# Revit family: HVAC_Air-Conditioning_Ice-Air_SPXC
name_source: partatom
category: Mechanical Equipment
units: mm (PartAtom-declared; Revit-internal decimal feet)

## family parameters
Always vertical = Yes
Cut with Voids When Loaded = No
OmniClass Number = 23.75.10.21.11
Part Type = Normal
Room Calculation Point = No
Round Connector Dimension = Use Diameter
Shared = No
Work Plane-Based = No

## types (12) — shared parameters
Description = SPXC Series Single Package Air Conditioner and Heat Pump
Drain Pipe Diameter = 1 "
Frequency = 60 Hz
HSPF = 9
Manufacturer = Ice Air
Outside Air = 60 CFM
Phase = 1
Power Factor = 1
Product Material = Ice Air - Metal - Aluminium
Product Page URL = https://www.ice-air.com
Supply Air Connection Width = 9.5 "
URL = https://www.ice-air.com
Voltage = 208 V
z_Supply Pipe Center = 2 "
zero-valued in all types: Default Elevation

## per-type parameters (varying)
- SPXC12-3.5kW: Airflow=400 CFM; Apparent Load=1040 VA; COP=3.5; COP @ -5°F=1.52; COP @ 10°F=2.04; COP @ 5°F=1.86; Cooling Capacity Range=9,700 - 16,700; Electric Heater=3500 VA; Electric Heater (A)=17 A; Energy Efficiency Rating=13; Heating Capacity @ -5°F=5,100; Heating Capacity @ 10°F=7,100; Heating Capacity @ 5°F=6,800; Heating Capacity Range=8,600 - 14,200; Heating Input=5 A; Heating Input (Watts)=955 W; Height=47 "; Length=23 "; MCA (with Electric Heat)=22.5; MOCP (with Electric Heat)=25; Sensible Cooling Capacity=9900 Btu/h; Supply Air Connection Depth=8.5 "; Total Cooling Capacity=11200 Btu/h; Total Heating Capacity=11400 Btu/h; Weight=1 kN; Width=23 "
- SPXC12-5.0kW: Airflow=400 CFM; Apparent Load=1040 VA; COP=3.5; COP @ -5°F=1.52; COP @ 10°F=2.04; COP @ 5°F=1.86; Cooling Capacity Range=9,700 - 16,700; Electric Heater=5000 VA; Electric Heater (A)=24 A; Energy Efficiency Rating=13; Heating Capacity @ -5°F=5,100; Heating Capacity @ 10°F=7,100; Heating Capacity @ 5°F=6,800; Heating Capacity Range=8,600 - 14,200; Heating Input=5 A; Heating Input (Watts)=955 W; Height=47 "; Length=23 "; MCA (with Electric Heat)=27.8; MOCP (with Electric Heat)=30; Sensible Cooling Capacity=9900 Btu/h; Supply Air Connection Depth=8.5 "; Total Cooling Capacity=11200 Btu/h; Total Heating Capacity=11400 Btu/h; Weight=1 kN; Width=23 "
- SPXC18-5.0kW: Airflow=600 CFM; Apparent Load=1456 VA; COP=3.3; COP @ -5°F=1.5; COP @ 10°F=1.99; COP @ 5°F=1.82; Cooling Capacity Range=10,500 - 19,500; Electric Heater=5000 VA; Electric Heater (A)=24 A; Energy Efficiency Rating=11; Heating Capacity @ -5°F=8,000; Heating Capacity @ 10°F=10,700; Heating Capacity @ 5°F=10,300; Heating Capacity Range=11,500 - 19,200; Heating Input=7 A; Heating Input (Watts)=1350 W; Height=47 "; Length=23 "; MCA (with Electric Heat)=28.7; MOCP (with Electric Heat)=30; Sensible Cooling Capacity=12900 Btu/h; Supply Air Connection Depth=8.5 "; Total Cooling Capacity=16800 Btu/h; Total Heating Capacity=15200 Btu/h; Weight=1.2 kN; Width=23 "
- SPXC18-7.5kW: Airflow=600 CFM; Apparent Load=1456 VA; COP=3.3; COP @ -5°F=1.5; COP @ 10°F=1.99; COP @ 5°F=1.82; Cooling Capacity Range=10,500 - 19,500; Electric Heater=7500 VA; Electric Heater (A)=36 A; Energy Efficiency Rating=11; Heating Capacity @ -5°F=8,000; Heating Capacity @ 10°F=10,700; Heating Capacity @ 5°F=10,300; Heating Capacity Range=11,500 - 19,200; Heating Input=7 A; Heating Input (Watts)=1350 W; Height=47 "; Length=23 "; MCA (with Electric Heat)=47.4; MOCP (with Electric Heat)=50; Sensible Cooling Capacity=12900 Btu/h; Supply Air Connection Depth=8.5 "; Total Cooling Capacity=16800 Btu/h; Total Heating Capacity=15200 Btu/h; Weight=1.2 kN; Width=23 "
- SPXC24-5.0kW: Airflow=800 CFM; Apparent Load=1872 VA; COP=3.3; COP @ -5°F=1.72; COP @ 10°F=2.18; COP @ 5°F=1.99; Cooling Capacity Range=13,900 - 25,600; Electric Heater=5000 VA; Electric Heater (A)=24 A; Energy Efficiency Rating=11; Heating Capacity @ -5°F=15,800; Heating Capacity @ 10°F=17,400; Heating Capacity @ 5°F=16,200; Heating Capacity Range=15,100 - 25,900; Heating Input=9 A; Heating Input (Watts)=1865 W; Height=64 "; Length=26 "; MCA (with Electric Heat)=28.9; MOCP (with Electric Heat)=30; Sensible Cooling Capacity=18500 Btu/h; Supply Air Connection Depth=10.63 "; Total Cooling Capacity=24000 Btu/h; Total Heating Capacity=21000 Btu/h; Weight=1.6 kN; Width=28 "
- SPXC24-7.5kW: Airflow=800 CFM; Apparent Load=1872 VA; COP=3.3; COP @ -5°F=1.72; COP @ 10°F=2.18; COP @ 5°F=1.99; Cooling Capacity Range=13,900 - 25,600; Electric Heater=7500 VA; Electric Heater (A)=36 A; Energy Efficiency Rating=11; Heating Capacity @ -5°F=15,800; Heating Capacity @ 10°F=17,400; Heating Capacity @ 5°F=16,200; Heating Capacity Range=15,100 - 25,900; Heating Input=9 A; Heating Input (Watts)=1865 W; Height=64 "; Length=26 "; MCA (with Electric Heat)=47.8; MOCP (with Electric Heat)=50; Sensible Cooling Capacity=18500 Btu/h; Supply Air Connection Depth=10.63 "; Total Cooling Capacity=24000 Btu/h; Total Heating Capacity=21000 Btu/h; Weight=1.6 kN; Width=28 "
- SPXC30-5.0kW: Airflow=1000 CFM; Apparent Load=2496 VA; COP=3.3; COP @ -5°F=1.69; COP @ 10°F=2.15; COP @ 5°F=1.96; Cooling Capacity Range=16,600 - 30,800; Electric Heater=5000 VA; Electric Heater (A)=24 A; Energy Efficiency Rating=11; Heating Capacity @ -5°F=19,300; Heating Capacity @ 10°F=21,300; Heating Capacity @ 5°F=19,800; Heating Capacity Range=18,000 - 31,500; Heating Input=12 A; Heating Input (Watts)=2509 W; Height=64 "; Length=26 "; MCA (with Electric Heat)=30.8; MOCP (with Electric Heat)=35; Sensible Cooling Capacity=22500 Btu/h; Supply Air Connection Depth=10.63 "; Total Cooling Capacity=27500 Btu/h; Total Heating Capacity=26000 Btu/h; Weight=1.7 kN; Width=28 "
- SPXC30-7.5kW: Airflow=1000 CFM; Apparent Load=2496 VA; COP=3.3; COP @ -5°F=1.69; COP @ 10°F=2.15; COP @ 5°F=1.96; Cooling Capacity Range=16,600 - 30,800; Electric Heater=7500 VA; Electric Heater (A)=36 A; Energy Efficiency Rating=11; Heating Capacity @ -5°F=19,300; Heating Capacity @ 10°F=21,300; Heating Capacity @ 5°F=19,800; Heating Capacity Range=18,000 - 31,500; Heating Input=12 A; Heating Input (Watts)=2509 W; Height=64 "; Length=26 "; MCA (with Electric Heat)=49.6; MOCP (with Electric Heat)=50; Sensible Cooling Capacity=22500 Btu/h; Supply Air Connection Depth=10.63 "; Total Cooling Capacity=27500 Btu/h; Total Heating Capacity=26000 Btu/h; Weight=1.7 kN; Width=28 "
- SPXC12: Airflow=400 CFM; Apparent Load=1040 VA; COP=3.5; COP @ -5°F=1.52; COP @ 10°F=2.04; COP @ 5°F=1.86; Cooling Capacity Range=9,700 - 16,700; Electric Heater=0 VA; Electric Heater (A)=0 A; Energy Efficiency Rating=13; Heating Capacity @ -5°F=5,100; Heating Capacity @ 10°F=7,100; Heating Capacity @ 5°F=6,800; Heating Capacity Range=8,600 - 14,200; Heating Input=5 A; Heating Input (Watts)=955 W; Height=47 "; Length=23 "; MCA (without Electric Heat)=9.8; MOCP (without Electric Heat)=15; Sensible Cooling Capacity=9900 Btu/h; Supply Air Connection Depth=8.5 "; Total Cooling Capacity=11200 Btu/h; Total Heating Capacity=11400 Btu/h; Weight=1 kN; Width=23 "
- SPXC18: Airflow=600 CFM; Apparent Load=1456 VA; COP=3.3; COP @ -5°F=1.5; COP @ 10°F=1.99; COP @ 5°F=1.82; Cooling Capacity Range=10,500 - 19,500; Electric Heater=0 VA; Electric Heater (A)=0 A; Energy Efficiency Rating=11; Heating Capacity @ -5°F=8,000; Heating Capacity @ 10°F=10,700; Heating Capacity @ 5°F=10,300; Heating Capacity Range=11,500 - 19,200; Heating Input=7 A; Heating Input (Watts)=1350 W; Height=47 "; Length=23 "; MCA (without Electric Heat)=14.8; MOCP (without Electric Heat)=20; Sensible Cooling Capacity=12900 Btu/h; Supply Air Connection Depth=8.5 "; Total Cooling Capacity=16800 Btu/h; Total Heating Capacity=15200 Btu/h; Weight=1.2 kN; Width=23 "
- SPXC24: Airflow=800 CFM; Apparent Load=1872 VA; COP=3.3; COP @ -5°F=1.72; COP @ 10°F=2.18; COP @ 5°F=1.99; Cooling Capacity Range=13,900 - 25,600; Electric Heater=0 VA; Electric Heater (A)=0 A; Energy Efficiency Rating=11; Heating Capacity @ -5°F=15,800; Heating Capacity @ 10°F=17,400; Heating Capacity @ 5°F=16,200; Heating Capacity Range=15,100 - 25,900; Heating Input=9 A; Heating Input (Watts)=1865 W; Height=64 "; Length=26 "; MCA (without Electric Heat)=18.8; MOCP (without Electric Heat)=25; Sensible Cooling Capacity=18500 Btu/h; Supply Air Connection Depth=10.63 "; Total Cooling Capacity=24000 Btu/h; Total Heating Capacity=21000 Btu/h; Weight=1.6 kN; Width=28 "
- SPXC30: Airflow=1000 CFM; Apparent Load=2496 VA; COP=3.3; COP @ -5°F=1.69; COP @ 10°F=2.15; COP @ 5°F=1.96; Cooling Capacity Range=16,600 - 30,800; Electric Heater=0 VA; Electric Heater (A)=0 A; Energy Efficiency Rating=11; Heating Capacity @ -5°F=19,300; Heating Capacity @ 10°F=21,300; Heating Capacity @ 5°F=19,800; Heating Capacity Range=18,000 - 31,500; Heating Input=12 A; Heating Input (Watts)=2509 W; Height=64 "; Length=26 "; MCA (without Electric Heat)=24.8; MOCP (without Electric Heat)=30; Sensible Cooling Capacity=22500 Btu/h; Supply Air Connection Depth=10.63 "; Total Cooling Capacity=27500 Btu/h; Total Heating Capacity=26000 Btu/h; Weight=1.7 kN; Width=28 "

note: column(s) folded — value = type name in every type: Model

## geometry (parser evidence)
native form markers: Sweep x2
no freeform markers — native parametric forms only
